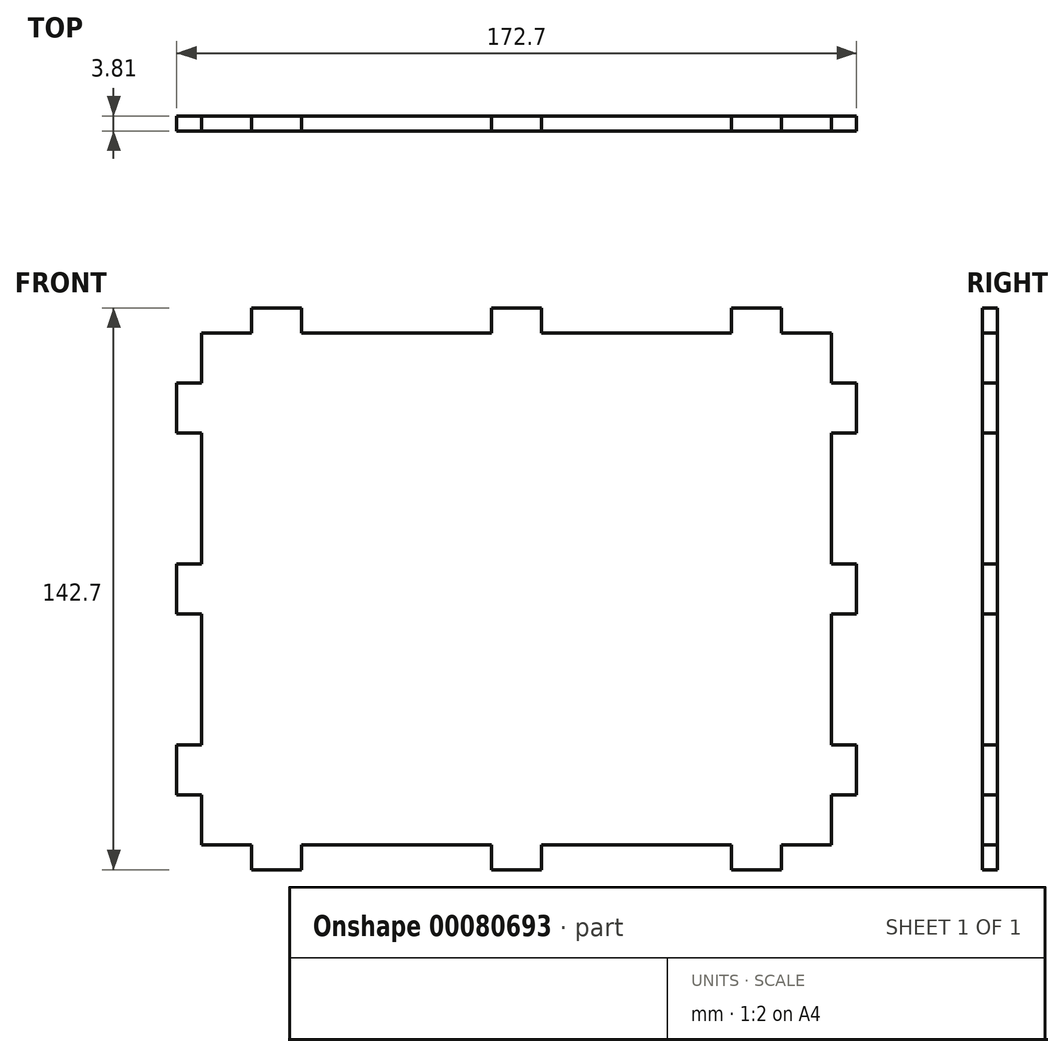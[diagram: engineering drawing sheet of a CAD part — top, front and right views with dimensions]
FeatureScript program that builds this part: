
annotation { "Feature Type Name" : "Feature", "Feature Type Description" : "" }
export const myFeature = defineFeature(function(context is Context, id is Id, definition is map)
    precondition{}
    {
        {
            var Q0;
            Q0=qCreatedBy(makeId("Front.planeOp"),FACE);
            var sketch = newSketch(context, id + "F0", { "sketchPlane" : qUnion([Q0])});
            skLineSegment(sketch, "E0.bottom", {"start": v(-197.85, -61.57) * mm, "end": v(-357.85, -61.57) * mm});
            skLineSegment(sketch, "E0.top", {"start": v(-197.85, 68.43) * mm, "end": v(-357.85, 68.43) * mm});
            skLineSegment(sketch, "E0.left", {"start": v(-197.85, -61.57) * mm, "end": v(-197.85, 68.43) * mm});
            skLineSegment(sketch, "E0.right", {"start": v(-357.85, -61.57) * mm, "end": v(-357.85, 68.43) * mm});
            skPoint(sketch, "E0.middle", {"position": v(-277.85, 3.43) * mm});
            skLineSegment(sketch, "E1.bottom", {"start": v(-271.5, 74.78) * mm, "end": v(-284.2, 74.78) * mm});
            skLineSegment(sketch, "E1.top", {"start": v(-271.5, 62.08) * mm, "end": v(-284.2, 62.08) * mm});
            skLineSegment(sketch, "E1.left", {"start": v(-271.5, 74.78) * mm, "end": v(-271.5, 62.08) * mm});
            skLineSegment(sketch, "E1.right", {"start": v(-284.2, 74.78) * mm, "end": v(-284.2, 62.08) * mm});
            skPoint(sketch, "E1.middle", {"position": v(-277.85, 68.43) * mm});
            skLineSegment(sketch, "E2.bottom", {"start": v(-223.25, 74.78) * mm, "end": v(-210.55, 74.78) * mm});
            skLineSegment(sketch, "E2.top", {"start": v(-223.25, 62.08) * mm, "end": v(-210.55, 62.08) * mm});
            skLineSegment(sketch, "E2.left", {"start": v(-223.25, 74.78) * mm, "end": v(-223.25, 62.08) * mm});
            skLineSegment(sketch, "E2.right", {"start": v(-210.55, 74.78) * mm, "end": v(-210.55, 62.08) * mm});
            skPoint(sketch, "E2.middle", {"position": v(-216.9, 68.43) * mm});
            skLineSegment(sketch, "E3.bottom", {"start": v(-332.45, 74.78) * mm, "end": v(-345.15, 74.78) * mm});
            skLineSegment(sketch, "E3.top", {"start": v(-332.45, 62.08) * mm, "end": v(-345.15, 62.08) * mm});
            skLineSegment(sketch, "E3.left", {"start": v(-332.45, 74.78) * mm, "end": v(-332.45, 62.08) * mm});
            skLineSegment(sketch, "E3.right", {"start": v(-345.15, 74.78) * mm, "end": v(-345.15, 62.08) * mm});
            skPoint(sketch, "E3.middle", {"position": v(-338.8, 68.43) * mm});
            skLineSegment(sketch, "E4.bottom", {"start": v(-364.2, 9.78) * mm, "end": v(-351.5, 9.78) * mm});
            skLineSegment(sketch, "E4.top", {"start": v(-364.2, -2.92) * mm, "end": v(-351.5, -2.92) * mm});
            skLineSegment(sketch, "E4.left", {"start": v(-364.2, 9.78) * mm, "end": v(-364.2, -2.92) * mm});
            skLineSegment(sketch, "E4.right", {"start": v(-351.5, 9.78) * mm, "end": v(-351.5, -2.92) * mm});
            skPoint(sketch, "E4.middle", {"position": v(-357.85, 3.43) * mm});
            skLineSegment(sketch, "E5.bottom", {"start": v(-364.2, 55.73) * mm, "end": v(-351.5, 55.73) * mm});
            skLineSegment(sketch, "E5.top", {"start": v(-364.2, 43.03) * mm, "end": v(-351.5, 43.03) * mm});
            skLineSegment(sketch, "E5.left", {"start": v(-364.2, 55.73) * mm, "end": v(-364.2, 43.03) * mm});
            skLineSegment(sketch, "E5.right", {"start": v(-351.5, 55.73) * mm, "end": v(-351.5, 43.03) * mm});
            skPoint(sketch, "E5.middle", {"position": v(-357.85, 49.38) * mm});
            skLineSegment(sketch, "E6", {"start": v(-277.85, 68.43) * mm, "end": v(-277.85, -61.57) * mm});
            skLineSegment(sketch, "E7.MirrorCS", {"start": v(-271.5, -55.22) * mm, "end": v(-284.2, -55.22) * mm});
            skLineSegment(sketch, "E8.MirrorCS", {"start": v(-284.2, -67.92) * mm, "end": v(-284.2, -55.22) * mm});
            skLineSegment(sketch, "E9.MirrorCS", {"start": v(-271.5, -67.92) * mm, "end": v(-284.2, -67.92) * mm});
            skLineSegment(sketch, "E10.MirrorCS", {"start": v(-271.5, -67.92) * mm, "end": v(-271.5, -55.22) * mm});
            skLineSegment(sketch, "E11.MirrorCS", {"start": v(-223.25, -67.92) * mm, "end": v(-223.25, -55.22) * mm});
            skLineSegment(sketch, "E12.MirrorCS", {"start": v(-223.25, -67.92) * mm, "end": v(-210.55, -67.92) * mm});
            skLineSegment(sketch, "E13.MirrorCS", {"start": v(-210.55, -67.92) * mm, "end": v(-210.55, -55.22) * mm});
            skLineSegment(sketch, "E14.MirrorCS", {"start": v(-223.25, -55.22) * mm, "end": v(-210.55, -55.22) * mm});
            skLineSegment(sketch, "E15.MirrorCS", {"start": v(-332.45, -55.22) * mm, "end": v(-345.15, -55.22) * mm});
            skLineSegment(sketch, "E16.MirrorCS", {"start": v(-332.45, -67.92) * mm, "end": v(-332.45, -55.22) * mm});
            skLineSegment(sketch, "E17.MirrorCS", {"start": v(-332.45, -67.92) * mm, "end": v(-345.15, -67.92) * mm});
            skLineSegment(sketch, "E18.MirrorCS", {"start": v(-345.15, -67.92) * mm, "end": v(-345.15, -55.22) * mm});
            skLineSegment(sketch, "E19.bottom", {"start": v(-364.2, -36.17) * mm, "end": v(-351.5, -36.17) * mm});
            skLineSegment(sketch, "E19.top", {"start": v(-364.2, -48.87) * mm, "end": v(-351.5, -48.87) * mm});
            skLineSegment(sketch, "E19.left", {"start": v(-364.2, -36.17) * mm, "end": v(-364.2, -48.87) * mm});
            skLineSegment(sketch, "E19.right", {"start": v(-351.5, -36.17) * mm, "end": v(-351.5, -48.87) * mm});
            skPoint(sketch, "E19.middle", {"position": v(-357.85, -42.52) * mm});
            skLineSegment(sketch, "E20.MirrorCS", {"start": v(-204.2, -36.17) * mm, "end": v(-204.2, -48.87) * mm});
            skLineSegment(sketch, "E21.MirrorCS", {"start": v(-191.5, -36.17) * mm, "end": v(-204.2, -36.17) * mm});
            skLineSegment(sketch, "E22.MirrorCS", {"start": v(-191.5, -36.17) * mm, "end": v(-191.5, -48.87) * mm});
            skLineSegment(sketch, "E23.MirrorCS", {"start": v(-191.5, -48.87) * mm, "end": v(-204.2, -48.87) * mm});
            skLineSegment(sketch, "E24.MirrorCS", {"start": v(-191.5, -2.92) * mm, "end": v(-204.2, -2.92) * mm});
            skLineSegment(sketch, "E25.MirrorCS", {"start": v(-204.2, 9.78) * mm, "end": v(-204.2, -2.92) * mm});
            skLineSegment(sketch, "E26.MirrorCS", {"start": v(-191.5, 9.78) * mm, "end": v(-204.2, 9.78) * mm});
            skLineSegment(sketch, "E27.MirrorCS", {"start": v(-191.5, 9.78) * mm, "end": v(-191.5, -2.92) * mm});
            skLineSegment(sketch, "E28.MirrorCS", {"start": v(-191.5, 43.03) * mm, "end": v(-204.2, 43.03) * mm});
            skLineSegment(sketch, "E29.MirrorCS", {"start": v(-191.5, 55.73) * mm, "end": v(-204.2, 55.73) * mm});
            skLineSegment(sketch, "E30.MirrorCS", {"start": v(-204.2, 55.73) * mm, "end": v(-204.2, 43.03) * mm});
            skLineSegment(sketch, "E31.MirrorCS", {"start": v(-191.5, 55.73) * mm, "end": v(-191.5, 43.03) * mm});
            skPoint(sketch, "E32.trimOffspring.end.orphan", {"position": v(-197.85, 3.43) * mm});
            skPoint(sketch, "E33.right.start.orphan", {"position": v(-300.44, 47.52) * mm});
            skPoint(sketch, "E33.left.start.orphan", {"position": v(-347.7, 47.52) * mm});
            skPoint(sketch, "E33.top.end.orphan", {"position": v(-300.44, -27.48) * mm});
            skPoint(sketch, "E33.top.start.orphan", {"position": v(-347.7, -27.48) * mm});
            skPoint(sketch, "E34.MirrorCS.end.orphan", {"position": v(-255.26, -27.48) * mm});
            skPoint(sketch, "E34.MirrorCS.start.orphan", {"position": v(-208.01, -27.48) * mm});
            skPoint(sketch, "E35.MirrorCS.start.orphan", {"position": v(-255.26, 47.52) * mm});
            skPoint(sketch, "E36.MirrorCS.start.orphan", {"position": v(-208.01, 47.52) * mm});
            skSolve(sketch);
        }
        {
            var Q0;
            {var subQ5=sQuery(id+"F0.wireOp",EDGE,"E5.right");Q0=makeQuery(id+"F0.imprint","IMPRINT",FACE,{"disambiguationData":[TD([[makeQuery(id+"F0.imprint","IMPRINT",EDGE,{"derivedFrom":subQ5}),-1.0]])]});}
            var Q1;
            {var subQ5=sQuery(id+"F0.wireOp",EDGE,"E5.left");Q1=makeQuery(id+"F0.imprint","IMPRINT",FACE,{"disambiguationData":[TD([[makeQuery(id+"F0.imprint","IMPRINT",EDGE,{"derivedFrom":subQ5}),1.0]])]});}
            var Q2;
            {var subQ0=sQuery(id+"F0.wireOp",EDGE,"E0.right");var subQ1=sQuery(id+"F0.wireOp",EDGE,"E0.top");var subQ2=makeQuery(id+"F0.imprint","INTERSECT",VERTEX,{"derivedFrom":[subQ1,subQ0]});Q2=makeQuery(id+"F0.imprint","IMPRINT",FACE,{"disambiguationData":[TD([[makeQuery(id+"F0.imprint","IMPRINT",EDGE,{"disambiguationData":[TD([[subQ2,1.0]])],"derivedFrom":subQ1}),1.0]])]});}
            var Q3;
            {var subQ5=sQuery(id+"F0.wireOp",EDGE,"E3.top");Q3=makeQuery(id+"F0.imprint","IMPRINT",FACE,{"disambiguationData":[TD([[makeQuery(id+"F0.imprint","IMPRINT",EDGE,{"derivedFrom":subQ5}),-1.0]])]});}
            var Q4;
            {var subQ5=sQuery(id+"F0.wireOp",EDGE,"E3.bottom");Q4=makeQuery(id+"F0.imprint","IMPRINT",FACE,{"disambiguationData":[TD([[makeQuery(id+"F0.imprint","IMPRINT",EDGE,{"derivedFrom":subQ5}),1.0]])]});}
            var Q5;
            {var subQ31=sQuery(id+"F0.wireOp",EDGE,"E1.top");Q5=makeQuery(id+"F0.imprint","IMPRINT",FACE,{"disambiguationData":[TD([[makeQuery(id+"F0.imprint","IMPRINT",EDGE,{"derivedFrom":subQ31}),1.0]])]});}
            var Q6;
            {var subQ5=sQuery(id+"F0.wireOp",EDGE,"E1.bottom");Q6=makeQuery(id+"F0.imprint","IMPRINT",FACE,{"disambiguationData":[TD([[makeQuery(id+"F0.imprint","IMPRINT",EDGE,{"derivedFrom":subQ5}),1.0]])]});}
            var Q7;
            {var subQ5=sQuery(id+"F0.wireOp",EDGE,"E1.top");Q7=makeQuery(id+"F0.imprint","IMPRINT",FACE,{"disambiguationData":[TD([[makeQuery(id+"F0.imprint","IMPRINT",EDGE,{"derivedFrom":subQ5}),-1.0]])]});}
            var Q8;
            {var subQ5=sQuery(id+"F0.wireOp",EDGE,"E2.bottom");Q8=makeQuery(id+"F0.imprint","IMPRINT",FACE,{"disambiguationData":[TD([[makeQuery(id+"F0.imprint","IMPRINT",EDGE,{"derivedFrom":subQ5}),-1.0]])]});}
            var Q9;
            {var subQ5=sQuery(id+"F0.wireOp",EDGE,"E2.top");Q9=makeQuery(id+"F0.imprint","IMPRINT",FACE,{"disambiguationData":[TD([[makeQuery(id+"F0.imprint","IMPRINT",EDGE,{"derivedFrom":subQ5}),1.0]])]});}
            var Q10;
            {var subQ0=sQuery(id+"F0.wireOp",EDGE,"E0.left");var subQ1=sQuery(id+"F0.wireOp",EDGE,"E0.top");var subQ2=makeQuery(id+"F0.imprint","INTERSECT",VERTEX,{"derivedFrom":[subQ1,subQ0]});Q10=makeQuery(id+"F0.imprint","IMPRINT",FACE,{"disambiguationData":[TD([[makeQuery(id+"F0.imprint","IMPRINT",EDGE,{"disambiguationData":[TD([[subQ2,-1.0]])],"derivedFrom":subQ1}),1.0]])]});}
            var Q11;
            {var subQ5=sQuery(id+"F0.wireOp",EDGE,"6e67ea2a-bf6c-4d8d-991e-4c9610f454840.MirrorCS");Q11=makeQuery(id+"F0.imprint","IMPRINT",FACE,{"disambiguationData":[TD([[makeQuery(id+"F0.imprint","IMPRINT",EDGE,{"derivedFrom":subQ5}),1.0]])]});}
            var Q12;
            {var subQ5=sQuery(id+"F0.wireOp",EDGE,"e7a02cae-3dec-4235-90d6-44147ae123860.MirrorCS");Q12=makeQuery(id+"F0.imprint","IMPRINT",FACE,{"disambiguationData":[TD([[makeQuery(id+"F0.imprint","IMPRINT",EDGE,{"derivedFrom":subQ5}),-1.0]])]});}
            var Q13;
            {var subQ5=sQuery(id+"F0.wireOp",EDGE,"b77bcf1b-6ed8-48e8-9d4e-b293c0d97bf70.MirrorCS");Q13=makeQuery(id+"F0.imprint","IMPRINT",FACE,{"disambiguationData":[TD([[makeQuery(id+"F0.imprint","IMPRINT",EDGE,{"derivedFrom":subQ5}),1.0]])]});}
            var Q14;
            {var subQ5=sQuery(id+"F0.wireOp",EDGE,"3d584175-bd42-42f6-9b5a-85d0e25869fe0.MirrorCS");Q14=makeQuery(id+"F0.imprint","IMPRINT",FACE,{"disambiguationData":[TD([[makeQuery(id+"F0.imprint","IMPRINT",EDGE,{"derivedFrom":subQ5}),-1.0]])]});}
            var Q15;
            {var subQ5=sQuery(id+"F0.wireOp",EDGE,"cdb6775e-2d37-4d6a-90fa-4eca167a4fed0.MirrorCS");Q15=makeQuery(id+"F0.imprint","IMPRINT",FACE,{"disambiguationData":[TD([[makeQuery(id+"F0.imprint","IMPRINT",EDGE,{"derivedFrom":subQ5}),1.0]])]});}
            var Q16;
            {var subQ5=sQuery(id+"F0.wireOp",EDGE,"1e18de7c-31cb-43aa-ab19-022ff6750b660.MirrorCS");Q16=makeQuery(id+"F0.imprint","IMPRINT",FACE,{"disambiguationData":[TD([[makeQuery(id+"F0.imprint","IMPRINT",EDGE,{"derivedFrom":subQ5}),-1.0]])]});}
            var Q17;
            {var subQ0=sQuery(id+"F0.wireOp",EDGE,"38f30ffd-d7d7-4048-a385-bb1ef51f31f00.MirrorCS");var subQ1=sQuery(id+"F0.wireOp",EDGE,"E0.left");var subQ2=makeQuery(id+"F0.imprint","INTERSECT",VERTEX,{"derivedFrom":[subQ1,subQ0]});Q17=makeQuery(id+"F0.imprint","IMPRINT",FACE,{"disambiguationData":[TD([[makeQuery(id+"F0.imprint","IMPRINT",EDGE,{"disambiguationData":[TD([[subQ2,-1.0]])],"derivedFrom":subQ1}),1.0]])]});}
            var Q18;
            {var subQ5=sQuery(id+"F0.wireOp",EDGE,"8c4a78ce-fe7b-4a0c-9cb1-67b932f80da20.MirrorCS");Q18=makeQuery(id+"F0.imprint","IMPRINT",FACE,{"disambiguationData":[TD([[makeQuery(id+"F0.imprint","IMPRINT",EDGE,{"derivedFrom":subQ5}),-1.0]])]});}
            var Q19;
            {var subQ5=sQuery(id+"F0.wireOp",EDGE,"665f2488-0e6a-4b9e-9c0d-889857a463930.MirrorCS");Q19=makeQuery(id+"F0.imprint","IMPRINT",FACE,{"disambiguationData":[TD([[makeQuery(id+"F0.imprint","IMPRINT",EDGE,{"derivedFrom":subQ5}),1.0]])]});}
            var Q20;
            {var subQ5=sQuery(id+"F0.wireOp",EDGE,"7cdf0428-d974-4590-92a7-2ffb3f6deecd0.MirrorCS");Q20=makeQuery(id+"F0.imprint","IMPRINT",FACE,{"disambiguationData":[TD([[makeQuery(id+"F0.imprint","IMPRINT",EDGE,{"derivedFrom":subQ5}),1.0]])]});}
            var Q21;
            {var subQ5=sQuery(id+"F0.wireOp",EDGE,"a4e31e00-16c8-444c-b41a-9d1313db8a300.MirrorCS");Q21=makeQuery(id+"F0.imprint","IMPRINT",FACE,{"disambiguationData":[TD([[makeQuery(id+"F0.imprint","IMPRINT",EDGE,{"derivedFrom":subQ5}),-1.0]])]});}
            var Q22;
            {var subQ0=sQuery(id+"F0.wireOp",EDGE,"23c010f1-1732-4b4f-a1bf-fdb20c1cfe8f0.MirrorCS");Q22=makeQuery(id+"F0.imprint","IMPRINT",FACE,{"disambiguationData":[TD([[makeQuery(id+"F0.imprint","IMPRINT",EDGE,{"derivedFrom":subQ0}),1.0]])]});}
            var Q23;
            {var subQ0=sQuery(id+"F0.wireOp",EDGE,"1db746d3-bed4-4ef7-9f53-c32ba9d8edd40.MirrorCS");Q23=makeQuery(id+"F0.imprint","IMPRINT",FACE,{"disambiguationData":[TD([[makeQuery(id+"F0.imprint","IMPRINT",EDGE,{"derivedFrom":subQ0}),-1.0]])]});}
            var Q24;
            {var subQ0=sQuery(id+"F0.wireOp",EDGE,"38f30ffd-d7d7-4048-a385-bb1ef51f31f00.MirrorCS");var subQ1=sQuery(id+"F0.wireOp",EDGE,"E0.right");var subQ2=makeQuery(id+"F0.imprint","INTERSECT",VERTEX,{"derivedFrom":[subQ1,subQ0]});Q24=makeQuery(id+"F0.imprint","IMPRINT",FACE,{"disambiguationData":[TD([[makeQuery(id+"F0.imprint","IMPRINT",EDGE,{"disambiguationData":[TD([[subQ2,-1.0]])],"derivedFrom":subQ1}),-1.0]])]});}
            var Q25;
            {var subQ5=sQuery(id+"F0.wireOp",EDGE,"631de5aa-dca1-49e2-99dd-c5ba14d8356f0.MirrorCS");Q25=makeQuery(id+"F0.imprint","IMPRINT",FACE,{"disambiguationData":[TD([[makeQuery(id+"F0.imprint","IMPRINT",EDGE,{"derivedFrom":subQ5}),1.0]])]});}
            var Q26;
            {var subQ5=sQuery(id+"F0.wireOp",EDGE,"4b58c554-b021-4d2c-8e63-d08e2fe331a00.MirrorCS");Q26=makeQuery(id+"F0.imprint","IMPRINT",FACE,{"disambiguationData":[TD([[makeQuery(id+"F0.imprint","IMPRINT",EDGE,{"derivedFrom":subQ5}),-1.0]])]});}
            var Q27;
            {var subQ5=sQuery(id+"F0.wireOp",EDGE,"E4.right");Q27=makeQuery(id+"F0.imprint","IMPRINT",FACE,{"disambiguationData":[TD([[makeQuery(id+"F0.imprint","IMPRINT",EDGE,{"derivedFrom":subQ5}),-1.0]])]});}
            var Q28;
            {var subQ5=sQuery(id+"F0.wireOp",EDGE,"E4.left");Q28=makeQuery(id+"F0.imprint","IMPRINT",FACE,{"disambiguationData":[TD([[makeQuery(id+"F0.imprint","IMPRINT",EDGE,{"derivedFrom":subQ5}),1.0]])]});}
            var Q29;
            {var subQ5=sQuery(id+"F0.wireOp",EDGE,"70ba0a8e-15ca-4af5-ad1e-aec15cda82ba0.MirrorCS");Q29=makeQuery(id+"F0.imprint","IMPRINT",FACE,{"disambiguationData":[TD([[makeQuery(id+"F0.imprint","IMPRINT",EDGE,{"derivedFrom":subQ5}),1.0]])]});}
            var Q30;
            {var subQ5=sQuery(id+"F0.wireOp",EDGE,"05116e00-459e-4e34-ad64-0683ffe88f100.MirrorCS");Q30=makeQuery(id+"F0.imprint","IMPRINT",FACE,{"disambiguationData":[TD([[makeQuery(id+"F0.imprint","IMPRINT",EDGE,{"derivedFrom":subQ5}),-1.0]])]});}
            var Q31;
            {var subQ5=sQuery(id+"F0.wireOp",EDGE,"6eea4c6f-bbe4-46e0-a570-8c34d712b9610.MirrorCS");Q31=makeQuery(id+"F0.imprint","IMPRINT",FACE,{"disambiguationData":[TD([[makeQuery(id+"F0.imprint","IMPRINT",EDGE,{"derivedFrom":subQ5}),-1.0]])]});}
            var Q32;
            {var subQ5=sQuery(id+"F0.wireOp",EDGE,"f1c2bbc9-7080-4b4f-8636-39eca44de4050.MirrorCS");Q32=makeQuery(id+"F0.imprint","IMPRINT",FACE,{"disambiguationData":[TD([[makeQuery(id+"F0.imprint","IMPRINT",EDGE,{"derivedFrom":subQ5}),1.0]])]});}
            var Q33;
            {var subQ5=sQuery(id+"F0.wireOp",EDGE,"E19.left");Q33=makeQuery(id+"F0.imprint","IMPRINT",FACE,{"disambiguationData":[TD([[makeQuery(id+"F0.imprint","IMPRINT",EDGE,{"derivedFrom":subQ5}),1.0]])]});}
            var Q34;
            {var subQ5=sQuery(id+"F0.wireOp",EDGE,"E17.MirrorCS");Q34=makeQuery(id+"F0.imprint","IMPRINT",FACE,{"disambiguationData":[TD([[makeQuery(id+"F0.imprint","IMPRINT",EDGE,{"derivedFrom":subQ5}),-1.0]])]});}
            var Q35;
            {var subQ5=sQuery(id+"F0.wireOp",EDGE,"E19.right");Q35=makeQuery(id+"F0.imprint","IMPRINT",FACE,{"disambiguationData":[TD([[makeQuery(id+"F0.imprint","IMPRINT",EDGE,{"derivedFrom":subQ5}),-1.0]])]});}
            var Q36;
            {var subQ5=sQuery(id+"F0.wireOp",EDGE,"E15.MirrorCS");Q36=makeQuery(id+"F0.imprint","IMPRINT",FACE,{"disambiguationData":[TD([[makeQuery(id+"F0.imprint","IMPRINT",EDGE,{"derivedFrom":subQ5}),1.0]])]});}
            var Q37;
            {var subQ0=sQuery(id+"F0.wireOp",EDGE,"E6");var subQ1=sQuery(id+"F0.wireOp",EDGE,"E0.bottom");var subQ2=makeQuery(id+"F0.imprint","INTERSECT",VERTEX,{"derivedFrom":[subQ1,subQ0]});Q37=makeQuery(id+"F0.imprint","IMPRINT",FACE,{"disambiguationData":[TD([[makeQuery(id+"F0.imprint","IMPRINT",EDGE,{"disambiguationData":[TD([[subQ2,-1.0]])],"derivedFrom":subQ1}),-1.0]])]});}
            var Q38;
            {var subQ0=sQuery(id+"F0.wireOp",EDGE,"E6");var subQ1=sQuery(id+"F0.wireOp",EDGE,"E0.bottom");var subQ2=makeQuery(id+"F0.imprint","INTERSECT",VERTEX,{"derivedFrom":[subQ1,subQ0]});Q38=makeQuery(id+"F0.imprint","IMPRINT",FACE,{"disambiguationData":[TD([[makeQuery(id+"F0.imprint","IMPRINT",EDGE,{"disambiguationData":[TD([[subQ2,1.0]])],"derivedFrom":subQ1}),-1.0]])]});}
            var Q39;
            {var subQ0=sQuery(id+"F0.wireOp",EDGE,"E9.MirrorCS");Q39=makeQuery(id+"F0.imprint","IMPRINT",FACE,{"disambiguationData":[TD([[makeQuery(id+"F0.imprint","IMPRINT",EDGE,{"derivedFrom":subQ0}),-1.0]])]});}
            var Q40;
            {var subQ5=sQuery(id+"F0.wireOp",EDGE,"E12.MirrorCS");Q40=makeQuery(id+"F0.imprint","IMPRINT",FACE,{"disambiguationData":[TD([[makeQuery(id+"F0.imprint","IMPRINT",EDGE,{"derivedFrom":subQ5}),1.0]])]});}
            var Q41;
            {var subQ5=sQuery(id+"F0.wireOp",EDGE,"E14.MirrorCS");Q41=makeQuery(id+"F0.imprint","IMPRINT",FACE,{"disambiguationData":[TD([[makeQuery(id+"F0.imprint","IMPRINT",EDGE,{"derivedFrom":subQ5}),-1.0]])]});}
            var Q42;
            {var subQ5=sQuery(id+"F0.wireOp",EDGE,"E20.MirrorCS");Q42=makeQuery(id+"F0.imprint","IMPRINT",FACE,{"disambiguationData":[TD([[makeQuery(id+"F0.imprint","IMPRINT",EDGE,{"derivedFrom":subQ5}),1.0]])]});}
            var Q43;
            {var subQ5=sQuery(id+"F0.wireOp",EDGE,"E22.MirrorCS");Q43=makeQuery(id+"F0.imprint","IMPRINT",FACE,{"disambiguationData":[TD([[makeQuery(id+"F0.imprint","IMPRINT",EDGE,{"derivedFrom":subQ5}),-1.0]])]});}
            var Q44;
            {var subQ5=sQuery(id+"F0.wireOp",EDGE,"E25.MirrorCS");Q44=makeQuery(id+"F0.imprint","IMPRINT",FACE,{"disambiguationData":[TD([[makeQuery(id+"F0.imprint","IMPRINT",EDGE,{"derivedFrom":subQ5}),1.0]])]});}
            var Q45;
            {var subQ5=sQuery(id+"F0.wireOp",EDGE,"E27.MirrorCS");Q45=makeQuery(id+"F0.imprint","IMPRINT",FACE,{"disambiguationData":[TD([[makeQuery(id+"F0.imprint","IMPRINT",EDGE,{"derivedFrom":subQ5}),-1.0]])]});}
            var Q46;
            {var subQ5=sQuery(id+"F0.wireOp",EDGE,"E30.MirrorCS");Q46=makeQuery(id+"F0.imprint","IMPRINT",FACE,{"disambiguationData":[TD([[makeQuery(id+"F0.imprint","IMPRINT",EDGE,{"derivedFrom":subQ5}),1.0]])]});}
            var Q47;
            {var subQ5=sQuery(id+"F0.wireOp",EDGE,"E31.MirrorCS");Q47=makeQuery(id+"F0.imprint","IMPRINT",FACE,{"disambiguationData":[TD([[makeQuery(id+"F0.imprint","IMPRINT",EDGE,{"derivedFrom":subQ5}),-1.0]])]});}
            extrude(context, id + "F1", {"entities" : qUnion([Q0, Q1, Q2, Q3, Q4, Q5, Q6, Q7, Q8, Q9, Q10, Q11, Q12, Q13, Q14, Q15, Q16, Q17, Q18, Q19, Q20, Q21, Q22, Q23, Q24, Q25, Q26, Q27, Q28, Q29, Q30, Q31, Q32, Q33, Q34, Q35, Q36, Q37, Q38, Q39, Q40, Q41, Q42, Q43, Q44, Q45, Q46, Q47]), "depth" : 3.8 * mm});
        }
    });
